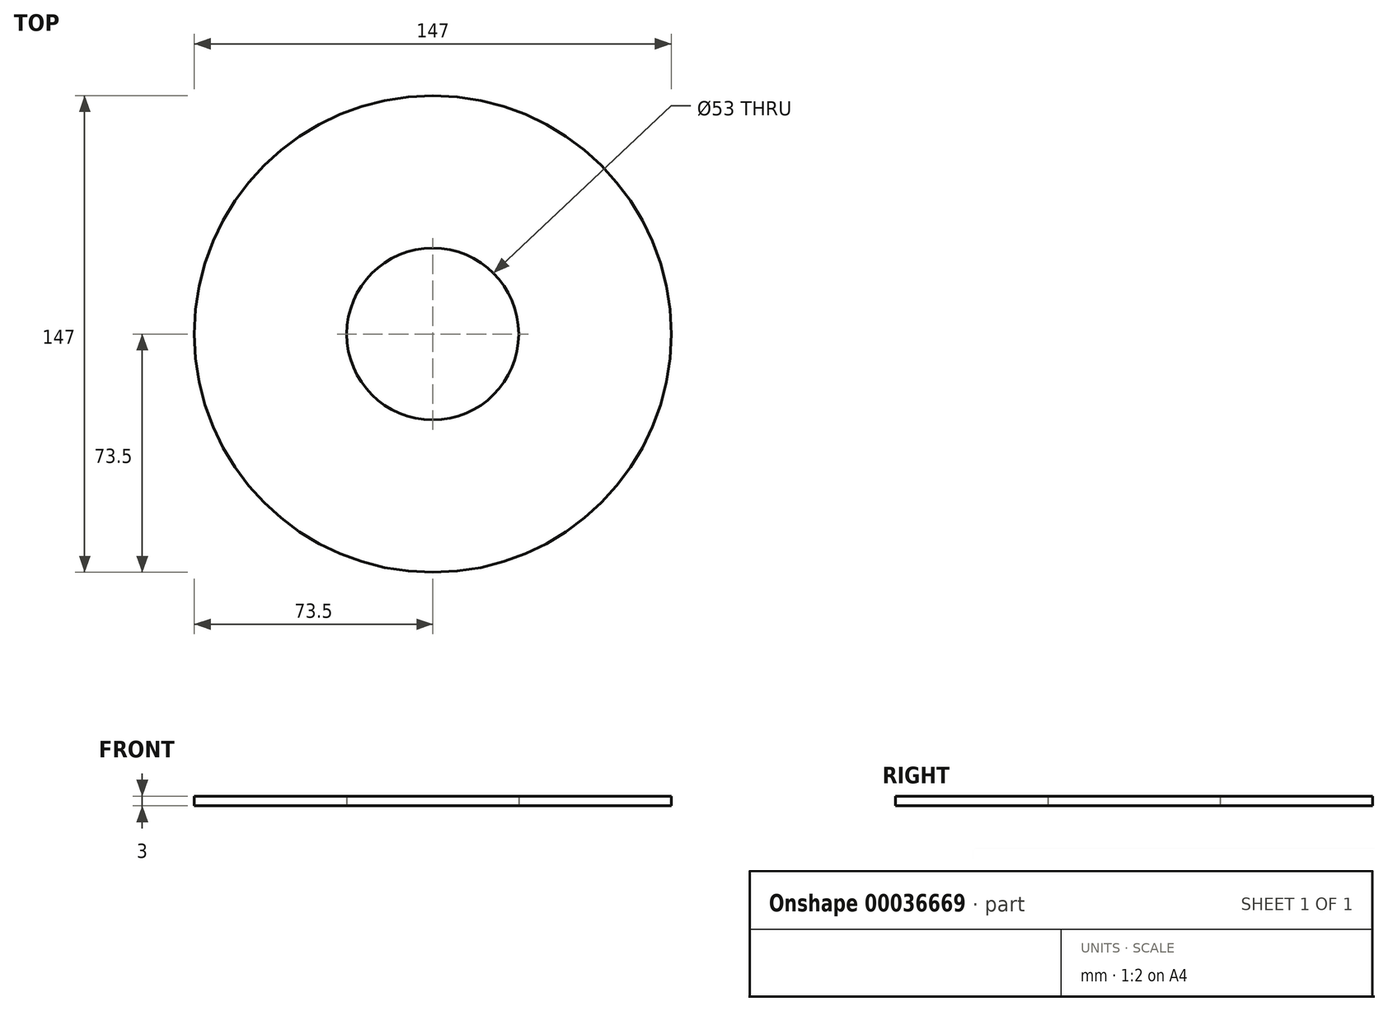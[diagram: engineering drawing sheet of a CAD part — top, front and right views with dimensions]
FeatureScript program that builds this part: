
annotation { "Feature Type Name" : "Feature", "Feature Type Description" : "" }
export const myFeature = defineFeature(function(context is Context, id is Id, definition is map)
    precondition{}
    {
        {
            var Q0;
            Q0=qCreatedBy(makeId("Top.planeOp"),FACE);
            var sketch = newSketch(context, id + "F0", { "sketchPlane" : qUnion([Q0])});
            skCircle(sketch, "E0", {"center": v(0, 0) * mm, "radius": 70.5 * mm});
            skCircle(sketch, "E1", {"center": v(0, 0) * mm, "radius": 73.5 * mm});
            skCircle(sketch, "E2", {"center": v(0, 0) * mm, "radius": 26.5 * mm});
            skSolve(sketch);
        }
        {
            var Q0;
            Q0=makeQuery(id+"F0.imprint","IMPRINT",FACE,{"disambiguationData":[TD([[makeQuery(id+"F0.imprint","IMPRINT",EDGE,{"derivedFrom":sQuery(id+"F0.wireOp",EDGE,"E0")}),1.0]])]});
            var Q1;
            Q1=makeQuery(id+"F0.imprint","IMPRINT",FACE,{"disambiguationData":[TD([[makeQuery(id+"F0.imprint","IMPRINT",EDGE,{"derivedFrom":sQuery(id+"F0.wireOp",EDGE,"E0")}),-1.0]])]});
            extrude(context, id + "F1", {"entities" : qUnion([Q0, Q1]), "depth" : 3 * mm});
        }
    });
